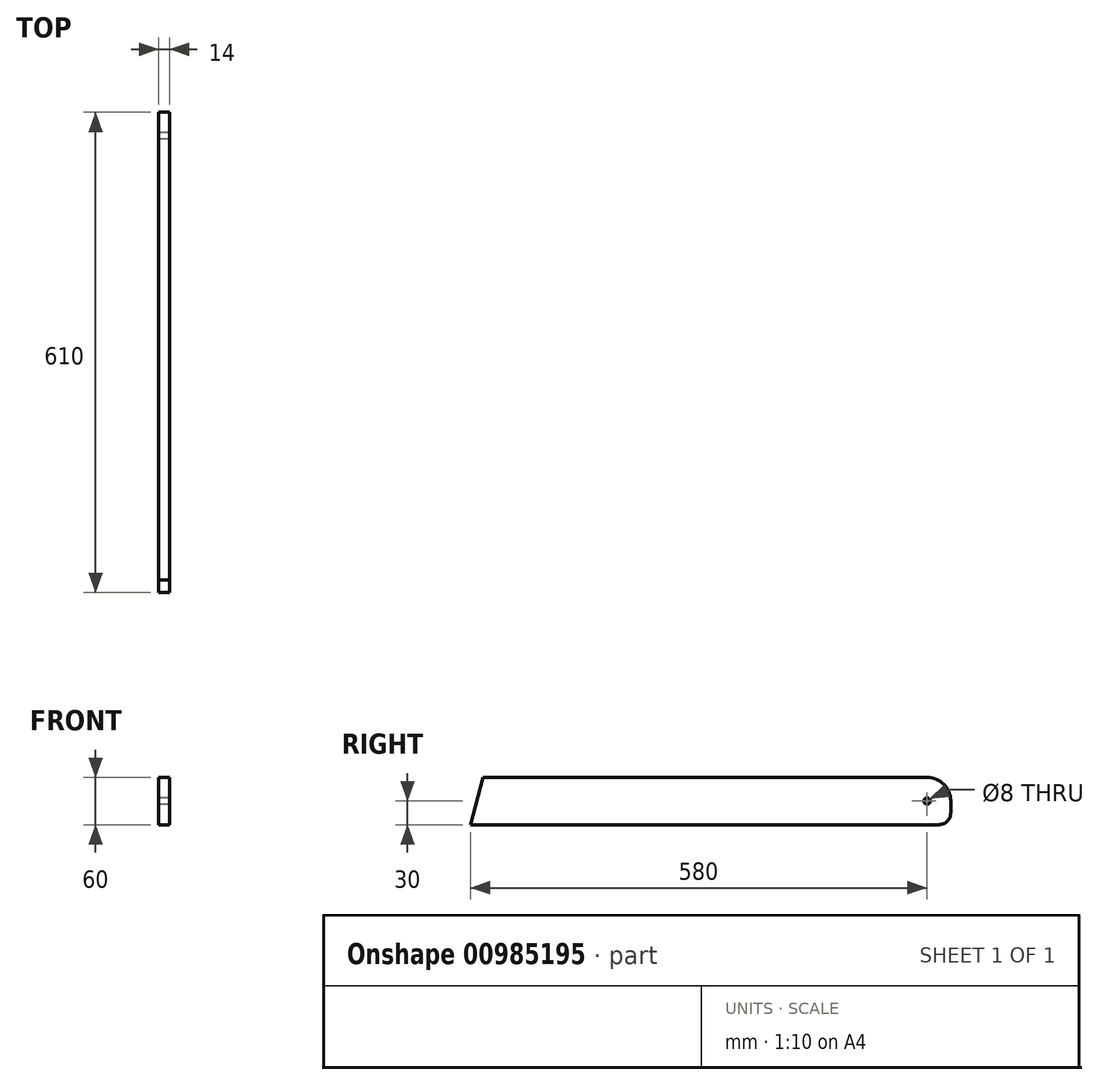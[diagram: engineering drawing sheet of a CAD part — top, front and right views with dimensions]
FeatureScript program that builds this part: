
annotation { "Feature Type Name" : "Feature", "Feature Type Description" : "" }
export const myFeature = defineFeature(function(context is Context, id is Id, definition is map)
    precondition{}
    {
        {
            var Q0;
            Q0=qCreatedBy(makeId("Right.planeOp"),FACE);
            var sketch = newSketch(context, id + "F0", { "sketchPlane" : qUnion([Q0])});
            skLineSegment(sketch, "E0.bottom", {"start": v(-288.92, 30) * mm, "end": v(275, 30) * mm});
            skLineSegment(sketch, "E0.top", {"start": v(-305, -30) * mm, "end": v(290, -30) * mm});
            skLineSegment(sketch, "E0.right", {"start": v(305, 0) * mm, "end": v(305, -15) * mm});
            skPoint(sketch, "E0.middle", {"position": v(0, 0) * mm});
            skLineSegment(sketch, "E1", {"start": v(-288.92, 30) * mm, "end": v(-305, -30) * mm});
            skPoint(sketch, "E2.visualSharp", {"position": v(305, 30) * mm});
            skArc(sketch, "E2.filletArc", {"start": v(305, 0) * mm, "mid": v(296.21, 21.21) * mm, "end": v(275, 30) * mm});
            skPoint(sketch, "E3.visualSharp", {"position": v(305, -30) * mm});
            skArc(sketch, "E3.filletArc", {"start": v(290, -30) * mm, "mid": v(300.6, -25.6) * mm, "end": v(305, -15) * mm});
            skSolve(sketch);
        }
        {
            var Q0;
            Q0=makeQuery(id+"F0.imprint","IMPRINT",FACE,{"disambiguationData":[TD([[makeQuery(id+"F0.imprint","IMPRINT",EDGE,{"derivedFrom":sQuery(id+"F0.wireOp",EDGE,"E0.bottom")}),-1.0]])]});
            extrude(context, id + "F1", {"entities" : qUnion([Q0]), "depth" : 14 * mm, "offsetDistance" : 25 * mm});
        }
        {
            var Q0;
            Q0=sQuery(id+"F0.wireOp",VERTEX,"E2.filletArc.center");
            var Q1;
            Q1=makeQuery(id+"F1.opExtrude","SWEPT_BODY",BODY,{"disambiguationData":[OSD([sQuery(id+"F0.wireOp",EDGE,"E0.bottom"),sQuery(id+"F0.wireOp",EDGE,"E0.top"),sQuery(id+"F0.wireOp",EDGE,"E0.right"),sQuery(id+"F0.wireOp",EDGE,"E1"),sQuery(id+"F0.wireOp",EDGE,"E2.filletArc"),sQuery(id+"F0.wireOp",EDGE,"E3.filletArc")])]});
            hole(context, id + "F2", {"style" : HoleStyle.SIMPLE, "endStyle" : HoleEndStyle.THROUGH, "oppositeDirection" : true, "holeDiameter" : 8 * mm, "majorDiameter" : 5 * mm, "isTappedThrough" : true, "tappedDepth" : 12 * mm, "tapClearance" : 3, "locations" : qUnion([Q0]), "scope" : qUnion([Q1])});
        }
    });
